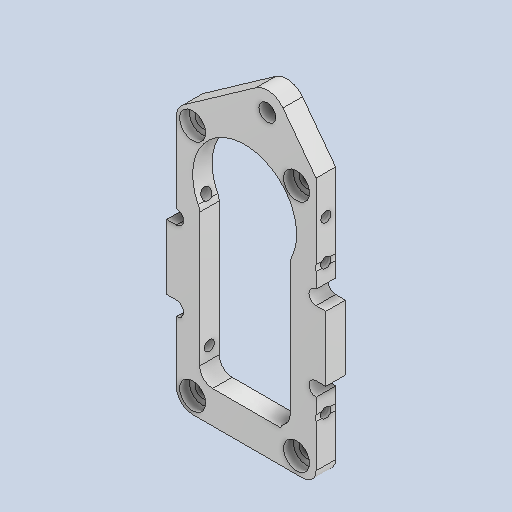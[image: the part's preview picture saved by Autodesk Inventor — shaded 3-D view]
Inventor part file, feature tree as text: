
AUTODESK INVENTOR PART (.ipt)
format: ipt  version: 2025.1 (Build 291241000, 241)  size: 427,008 bytes
history: native  units: mm
features: sketch x16, extrude x13, reference x11, other x9, fillet x4, hole x3, projected_geometry x2
ambient origin geometry x8: Origin, YZ Plane, XZ Plane, XY Plane, X Axis, Y Axis, Z Axis, Center Point
bodies: Body1 (feature_tree)
feature tree (58):
  other  "ソリッド1"
  extrude  "押し出し1"  Depth=2.2mm
  extrude  "押し出し2"  Depth=5.0mm
  extrude  "押し出し3"  Depth=2.2mm
  fillet  "フィレット1"  Radius=5.0mm
  hole  "穴1"  [1 undecoded]
  extrude  "押し出し4"  Depth=10.0mm
  extrude  "押し出し5"  Depth=3.0mm TaperAngle=0.0deg
  fillet  "フィレット2"  Radius=13.0mm
  extrude  "押し出し8"  Depth=6.0mm
  fillet  "フィレット4"  Radius=2.2mm
  extrude  "押し出し9"  Depth=5.0mm
  extrude  "押し出し10"  Depth=3.0mm
  hole  "穴2"  [1 undecoded]
  extrude  "押し出し11"  Depth=4.0mm
  extrude  "押し出し12"  Depth=4.0mm
  extrude  "押し出し13"  Depth=1.5mm TaperAngle=0.0deg
  hole  "穴3"  [1 undecoded]
  extrude  "押し出し6"  TaperAngle=0.0deg  [1 undecoded]
  extrude  "押し出し7"  Depth=2.0mm
  fillet  "フィレット3"  Radius=12.0mm
  sketch  "スケッチ1"
  reference  "参照1"
  reference  "参照2"
  reference  "参照3"
  reference  "参照4"
  reference  "参照5"
  sketch  "スケッチ3"
  sketch  "スケッチ4"
  reference  "参照6"
  reference  "参照7"
  reference  "参照8"
  projected_geometry  "投影ループ1"
  sketch  "スケッチ5"
  sketch  "スケッチ6"
  sketch  "スケッチ7"
  reference  "参照9"
  sketch  "スケッチ8"
  sketch  "スケッチ9"
  projected_geometry  "投影ループ2"
  sketch  "スケッチ10"
  reference  "参照10"
  sketch  "スケッチ11"
  sketch  "スケッチ12"
  sketch  "スケッチ13"
  sketch  "スケッチ14"
  sketch  "スケッチ15"
  sketch  "スケッチ16"
  sketch  "スケッチ17"
  reference  "参照11"
  other  "<userpath>\Documents\Inventor\Vixen\hizadati_vixen.iam"
  other  "hizadati_vixen.iam"
  other  "KRS2500_scale:7"
  other  "<userpath>\Documents\Inventor\Vixen\doutai.iam"
  other  "doutai.iam"
  other  "02157_SmallDiameterHornB:3"
  other  "namida:1"
  other  "kosiue:1"
note: 4 required parameter values undecoded (feature->parameter linkage not recoverable at this tier; creation-order binding heuristic only, values carry confidence <= 0.55)
